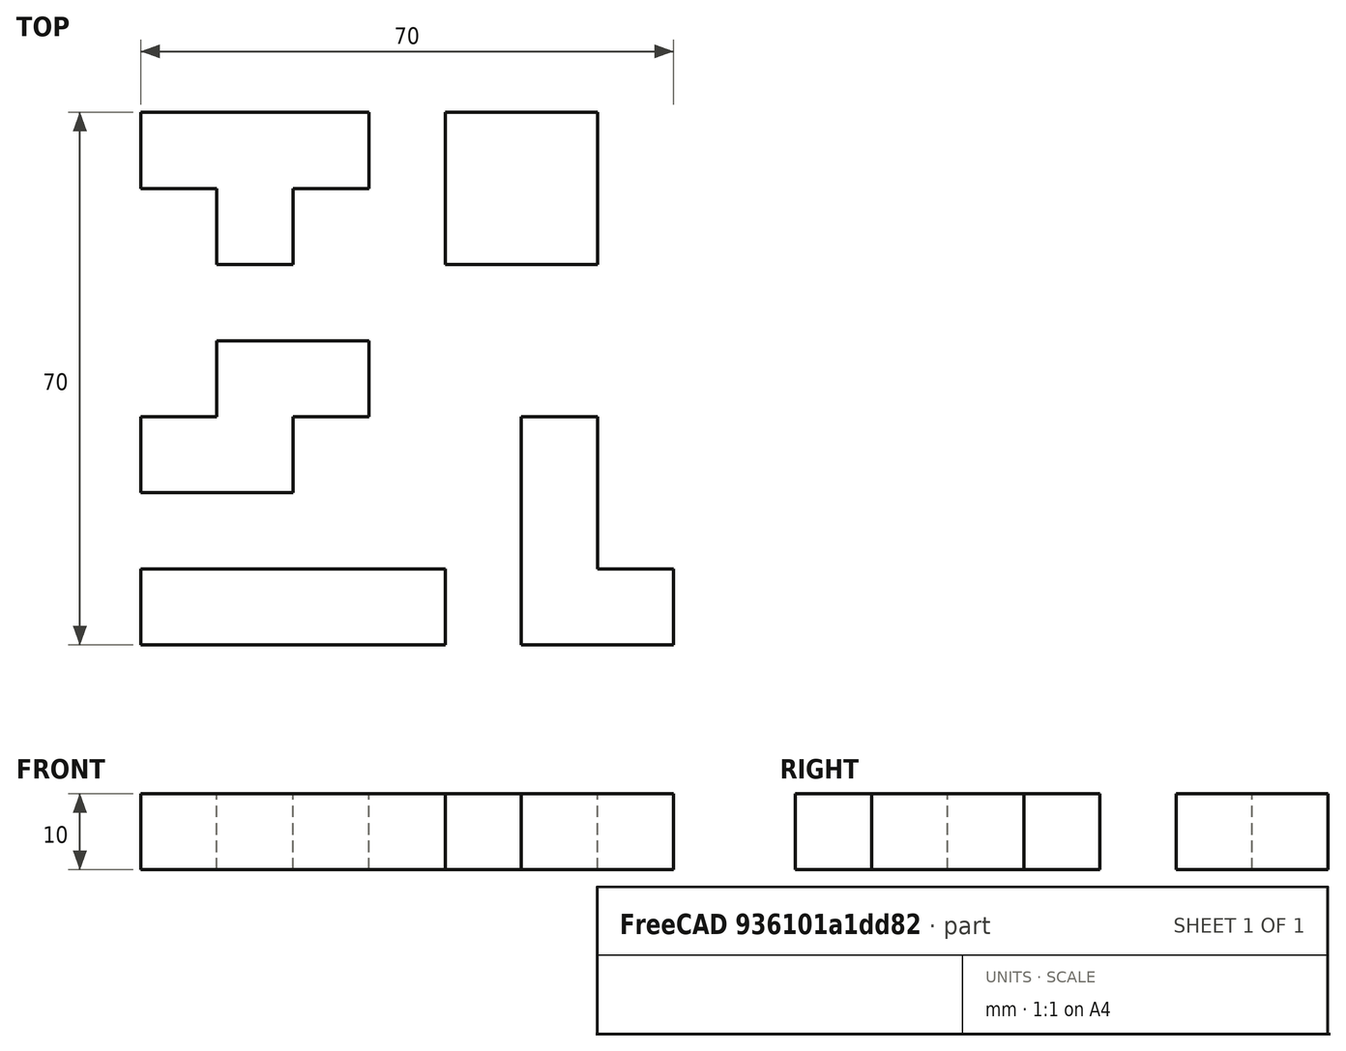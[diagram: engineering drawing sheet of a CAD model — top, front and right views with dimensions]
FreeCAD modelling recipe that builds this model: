
FCSTD DOCUMENT
Label: piezas-tetris
objects: Part::Box×8, Part::MultiFuse×3
note: 11 computed .brp shape members not serialized (recipe doc carries the construction recipe); baked Part::Feature solids carry a one-line shape summary decoded from their .brp

FEATURE [Part::Box] Box  label="Pieza-1"
  Height = 10
  Length = 40
  Placement = pos=(0,-20,0) rot=(0,0,1;0rad)
  Width = 10
FEATURE [Part::Box] Box001  label="Cubo-1"
  Height = 10
  Length = 30
  Width = 10
FEATURE [Part::Box] Box002  label="Cubo-2"
  Height = 10
  Length = 10
  Placement = pos=(10,-10,0) rot=(0,0,1;0rad)
  Width = 10
FEATURE [Part::MultiFuse] Fusion  label="Pieza-2"
  Placement = pos=(0,40,0) rot=(0,0,1;0rad)
  Shapes = -> [Box001,Box002]
FEATURE [Part::Box] Box003  label="Pieza-3"
  Height = 10
  Length = 20
  Placement = pos=(40,30,0) rot=(0,0,1;0rad)
  Width = 20
FEATURE [Part::Box] Box004  label="P4-cubo-1"
  Height = 10
  Length = 10
  Width = 30
FEATURE [Part::Box] Box005  label="P4-cubo-2"
  Height = 10
  Length = 10
  Placement = pos=(10,0,0) rot=(0,0,1;0rad)
  Width = 10
FEATURE [Part::MultiFuse] Fusion001  label="Pieza-4"
  Placement = pos=(50,-20,0) rot=(0,0,1;0rad)
  Shapes = -> [Box004,Box005]
FEATURE [Part::Box] Box006  label="P5-cubo1"
  Height = 10
  Length = 20
  Width = 10
FEATURE [Part::Box] Box007  label="P5-cubo2"
  Height = 10
  Length = 20
  Placement = pos=(10,10,0) rot=(0,0,1;0rad)
  Width = 10
FEATURE [Part::MultiFuse] Fusion002  label="Pieza-5"
  Shapes = -> [Box006,Box007]
